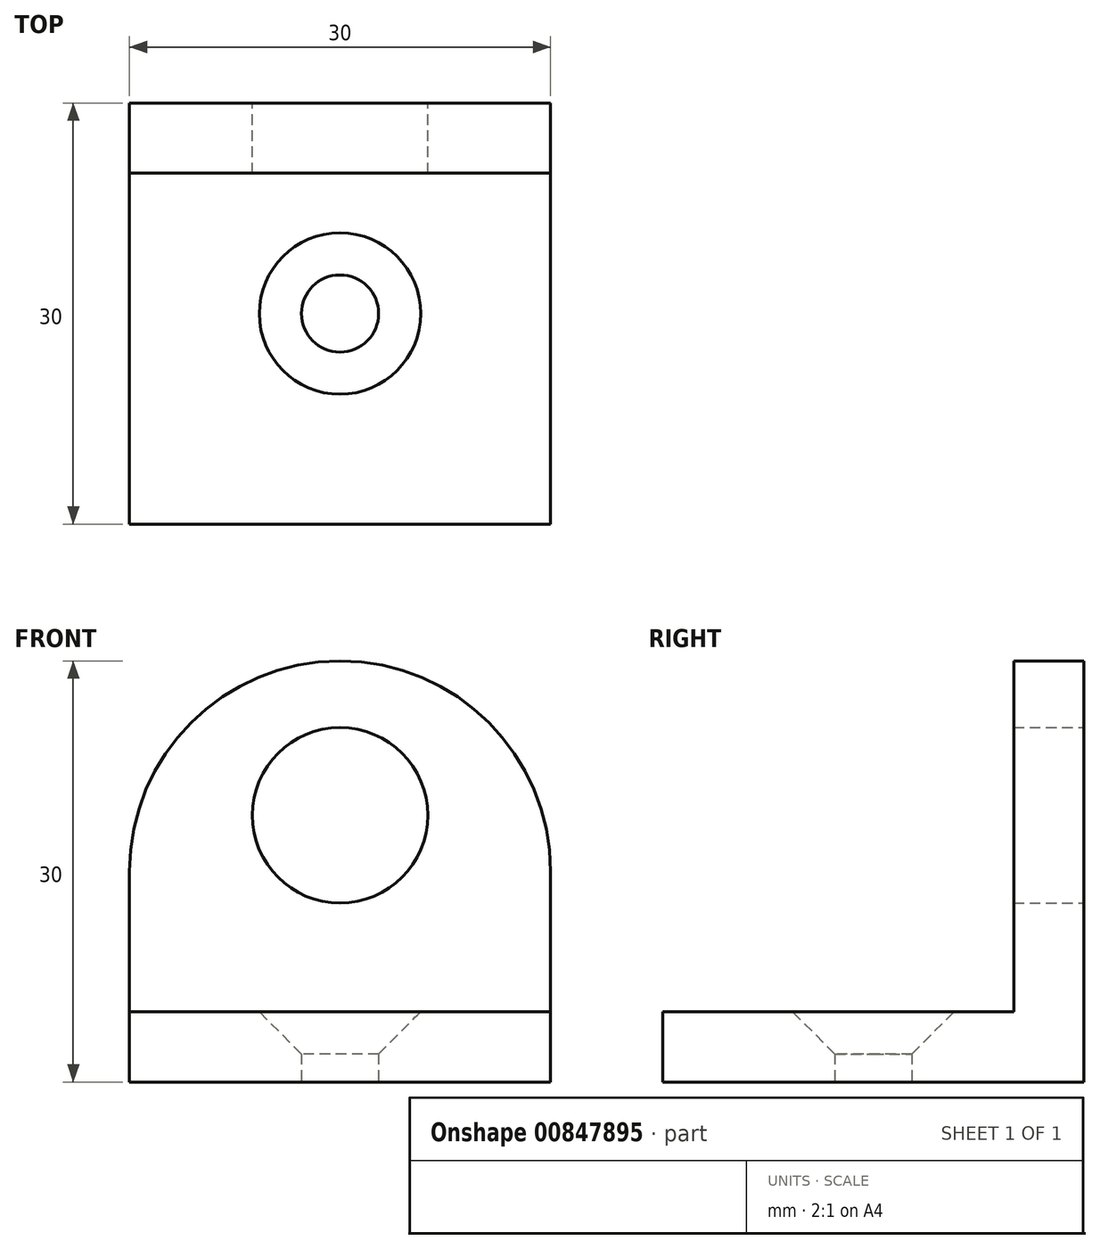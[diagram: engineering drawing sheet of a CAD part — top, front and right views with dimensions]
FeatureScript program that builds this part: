
annotation { "Feature Type Name" : "Feature", "Feature Type Description" : "" }
export const myFeature = defineFeature(function(context is Context, id is Id, definition is map)
    precondition{}
    {
        {
            var Q0;
            Q0=qCreatedBy(makeId("Top.planeOp"),FACE);
            var sketch = newSketch(context, id + "F0", { "sketchPlane" : qUnion([Q0])});
            skLineSegment(sketch, "E0.bottom", {"start": v(0, 13.28) * mm, "end": v(30, 13.28) * mm});
            skLineSegment(sketch, "E0.top", {"start": v(0, -16.72) * mm, "end": v(30, -16.72) * mm});
            skLineSegment(sketch, "E0.left", {"start": v(0, 13.28) * mm, "end": v(0, -16.72) * mm});
            skLineSegment(sketch, "E0.right", {"start": v(30, 13.28) * mm, "end": v(30, -16.72) * mm});
            skLineSegment(sketch, "E1", {"start": v(30, -16.72) * mm, "end": v(15, -16.72) * mm, "construction": true});
            skLineSegment(sketch, "E2", {"start": v(15, -16.72) * mm, "end": v(15, -1.72) * mm, "construction": true});
            skCircle(sketch, "E3", {"center": v(15, -1.72) * mm, "radius": 2.75 * mm});
            skSolve(sketch);
        }
        {
            var Q0;
            Q0 = qSketchRegion(id + "F0", true);
            extrude(context, id + "F1", {"entities" : qUnion([Q0]), "depth" : 5 * mm, "offsetDistance" : 25 * mm});
        }
        {
            var Q0;
            Q0=makeQuery(id+"F1.opExtrude","SWEPT_FACE",FACE,{"disambiguationData":[OSD([sQuery(id+"F0.wireOp",EDGE,"E0.bottom")])]});
            var sketch = newSketch(context, id + "F2", { "sketchPlane" : qUnion([Q0])});
            skLineSegment(sketch, "E4.bottom", {"start": v(0, 0) * mm, "end": v(-30, 0) * mm});
            skLineSegment(sketch, "E4.top", {"start": v(0, 30) * mm, "end": v(-30, 30) * mm});
            skLineSegment(sketch, "E4.left", {"start": v(0, 0) * mm, "end": v(0, 30) * mm});
            skLineSegment(sketch, "E4.right", {"start": v(-30, 0) * mm, "end": v(-30, 30) * mm});
            skSolve(sketch);
        }
        {
            var Q0;
            Q0 = qSketchRegion(id + "F2", true);
            extrude(context, id + "F3", {"entities" : qUnion([Q0]), "operationType" : NewBodyOperationType.ADD, "oppositeDirection" : true, "depth" : 5 * mm, "offsetDistance" : 25 * mm});
        }
        {
            var Q0;
            Q0=makeQuery(id+"F3.boolean.opBoolean","MERGE",FACE,{"derivedFrom":[makeQuery(id+"F1.opExtrude","SWEPT_FACE",FACE,{"disambiguationData":[OSD([sQuery(id+"F0.wireOp",EDGE,"E0.bottom")])]}),makeQuery(id+"F3.opExtrude","CAP_FACE",FACE,{"disambiguationData":[OSD([sQuery(id+"F2.wireOp",EDGE,"E4.bottom"),sQuery(id+"F2.wireOp",EDGE,"E4.top"),sQuery(id+"F2.wireOp",EDGE,"E4.left"),sQuery(id+"F2.wireOp",EDGE,"E4.right")])],"isStart":true})]});
            var sketch = newSketch(context, id + "F4", { "sketchPlane" : qUnion([Q0])});
            skLineSegment(sketch, "E5", {"start": v(-30, 30) * mm, "end": v(-15, 30) * mm, "construction": true});
            skLineSegment(sketch, "E6", {"start": v(-15, 30) * mm, "end": v(-15, 25) * mm, "construction": true});
            skLineSegment(sketch, "E7", {"start": v(-15, 25) * mm, "end": v(-15, 19) * mm, "construction": true});
            skCircle(sketch, "E8", {"center": v(-15, 19) * mm, "radius": 6.25 * mm});
            skSolve(sketch);
        }
        {
            var Q0;
            Q0 = qSketchRegion(id + "F4", true);
            extrude(context, id + "F5", {"entities" : qUnion([Q0]), "operationType" : NewBodyOperationType.REMOVE, "oppositeDirection" : true, "depth" : 6 * mm, "offsetDistance" : 25 * mm});
        }
        {
            var Q0;
            Q0=makeQuery(id+"F3.opExtrude","SWEPT_EDGE",EDGE,{"disambiguationData":[OSD([sQuery(id+"F2.wireOp",EDGE,"E4.top"),sQuery(id+"F2.wireOp",EDGE,"E4.right")])]});
            var Q1;
            Q1=makeQuery(id+"F3.opExtrude","SWEPT_EDGE",EDGE,{"disambiguationData":[OSD([sQuery(id+"F2.wireOp",EDGE,"E4.top"),sQuery(id+"F2.wireOp",EDGE,"E4.left")])]});
            fillet(context, id + "F6", {"entities" : qUnion([Q0, Q1]), "radius" : 15 * mm, "tangentPropagation" : true, "allowEdgeOverflow" : false});
        }
        {
            var Q0;
            Q0=makeQuery(id+"F1.opExtrude","CAP_EDGE",EDGE,{"disambiguationData":[OSD([sQuery(id+"F0.wireOp",EDGE,"E3")])],"isStart":false});
            chamfer(context, id + "F7", {"entities" : qUnion([Q0]), "width" : 3 * mm, "tangentPropagation" : true});
        }
    });
